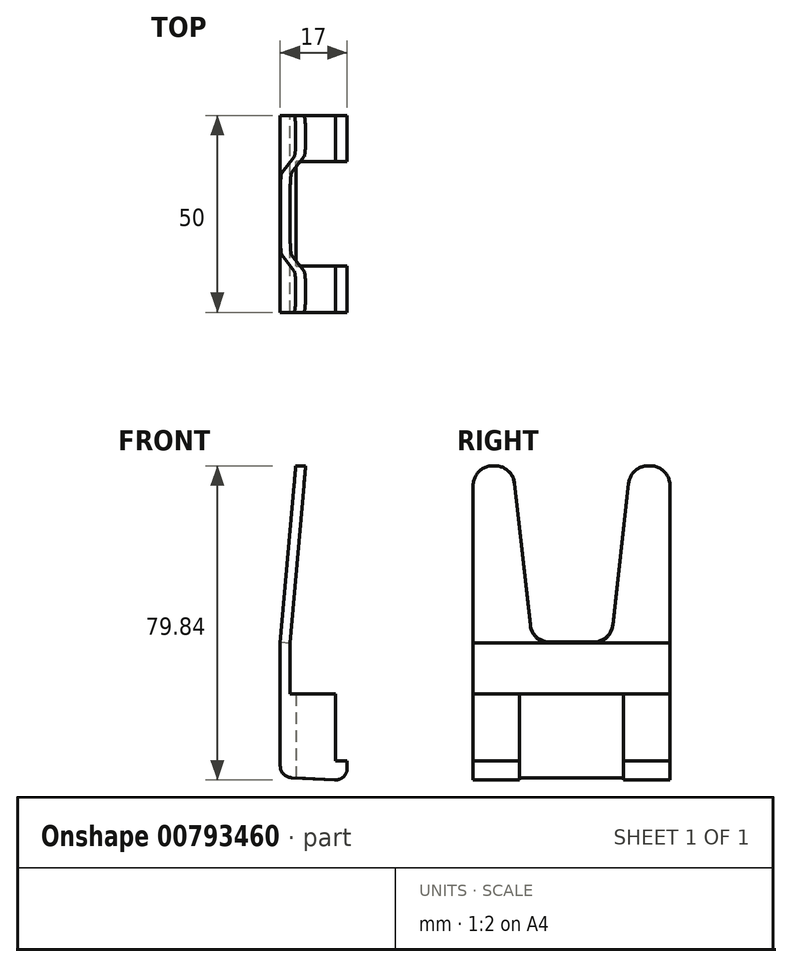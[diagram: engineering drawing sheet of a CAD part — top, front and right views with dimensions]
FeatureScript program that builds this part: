
annotation { "Feature Type Name" : "Feature", "Feature Type Description" : "" }
export const myFeature = defineFeature(function(context is Context, id is Id, definition is map)
    precondition{}
    {
        {
            var Q0;
            Q0=qCreatedBy(makeId("Front.planeOp"),FACE);
            var sketch = newSketch(context, id + "F0", { "sketchPlane" : qUnion([Q0])});
            skLineSegment(sketch, "E0", {"start": v(0, 0.9) * mm, "end": v(0, 35) * mm});
            skLineSegment(sketch, "E1", {"start": v(2.5, 35) * mm, "end": v(2.5, 22) * mm});
            skLineSegment(sketch, "E2", {"start": v(2.5, 22) * mm, "end": v(14, 22) * mm});
            skLineSegment(sketch, "E3", {"start": v(14, 22) * mm, "end": v(14, 5) * mm});
            skLineSegment(sketch, "E4", {"start": v(14, 5) * mm, "end": v(17, 5) * mm});
            skLineSegment(sketch, "E5", {"start": v(17, 5) * mm, "end": v(17, 0) * mm});
            skLineSegment(sketch, "E6", {"start": v(17, 0) * mm, "end": v(0, 0.9) * mm});
            skLineSegment(sketch, "E7", {"start": v(-12.07, 35) * mm, "end": v(18.84, 35) * mm, "construction": true});
            skLineSegment(sketch, "E8", {"start": v(0, 35) * mm, "end": v(3.94, 80) * mm});
            skLineSegment(sketch, "E9", {"start": v(3.94, 80) * mm, "end": v(6.44, 80) * mm});
            skLineSegment(sketch, "E10", {"start": v(6.44, 80) * mm, "end": v(2.5, 35) * mm});
            skSolve(sketch);
        }
        {
            var Q0;
            Q0 = qSketchRegion(id + "F0", true);
            extrude(context, id + "F1", {"entities" : qUnion([Q0]), "depth" : 50 * mm, "offsetDistance" : 25 * mm});
        }
        {
            var Q0;
            Q0=makeQuery(id+"F1.opExtrude","SWEPT_FACE",FACE,{"disambiguationData":[OSD([sQuery(id+"F0.wireOp",EDGE,"E5")])]});
            var sketch = newSketch(context, id + "F2", { "sketchPlane" : qUnion([Q0])});
            skLineSegment(sketch, "E11.bottom", {"start": v(-11.75, 34.94) * mm, "end": v(-38.25, 34.94) * mm});
            skLineSegment(sketch, "E11.top", {"start": v(-11.75, -24.94) * mm, "end": v(-38.25, -24.94) * mm});
            skLineSegment(sketch, "E11.left", {"start": v(-11.75, 34.94) * mm, "end": v(-11.75, -24.94) * mm});
            skLineSegment(sketch, "E11.right", {"start": v(-38.25, 34.94) * mm, "end": v(-38.25, -24.94) * mm});
            skPoint(sketch, "E11.middle", {"position": v(-25, 5) * mm});
            skSolve(sketch);
        }
        {
            var Q0;
            {var subQ0=sQuery(id+"F2.wireOp",EDGE,"E11.bottom");Q0=makeQuery(id+"F2.imprint","IMPRINT",FACE,{"disambiguationData":[TD([[makeQuery(id+"F2.imprint","IMPRINT",EDGE,{"derivedFrom":subQ0}),1.0]])]});}
            var Q1;
            {var subQ0=sQuery(id+"F2.wireOp",EDGE,"E11.left");var subQ1=sQuery(id+"F0.wireOp",EDGE,"E5");var subQ2=makeQuery(id+"F1.opExtrude","SWEPT_EDGE",EDGE,{"disambiguationData":[OSD([sQuery(id+"F0.wireOp",EDGE,"E4"),subQ1])]});var subQ3=makeQuery(id+"F2.imprint","INTERSECT",VERTEX,{"derivedFrom":[subQ2,subQ0]});Q1=makeQuery(id+"F2.imprint","IMPRINT",FACE,{"disambiguationData":[TD([[makeQuery(id+"F2.imprint","IMPRINT",EDGE,{"disambiguationData":[TD([[subQ3,-1.0]])],"derivedFrom":subQ0}),-1.0]])]});}
            extrude(context, id + "F3", {"entities" : qUnion([Q0, Q1]), "operationType" : NewBodyOperationType.REMOVE, "oppositeDirection" : true, "depth" : 13 * mm, "offsetDistance" : 25 * mm});
        }
        {
            var Q0;
            Q0=makeQuery(id+"F3.boolean.opBoolean","MERGE",FACE,{"derivedFrom":[makeQuery(id+"F1.opExtrude","SWEPT_FACE",FACE,{"disambiguationData":[OSD([sQuery(id+"F0.wireOp",EDGE,"E1")])]}),makeQuery(id+"F3.opExtrude","CAP_FACE",FACE,{"disambiguationData":[OSD([sQuery(id+"F0.wireOp",EDGE,"E5"),sQuery(id+"F0.wireOp",EDGE,"ma2ZBqUt-ZaSP-WYbq-Jd49-SRVpUCsUzQty"),sQuery(id+"F2.wireOp",EDGE,"E11.bottom"),sQuery(id+"F2.wireOp",EDGE,"E11.left"),sQuery(id+"F2.wireOp",EDGE,"E11.right")])],"isStart":false})]});
            var sketch = newSketch(context, id + "F4", { "sketchPlane" : qUnion([Q0])});
            skLineSegment(sketch, "E12", {"start": v(-15.42, 29.58) * mm, "end": v(-10, 35) * mm});
            skLineSegment(sketch, "E13", {"start": v(-25, 29.58) * mm, "end": v(-25, 92.21) * mm, "construction": true});
            skLineSegment(sketch, "E14.MirrorCS", {"start": v(-34.58, 29.58) * mm, "end": v(-40, 35) * mm});
            skLineSegment(sketch, "E15", {"start": v(-40, 35) * mm, "end": v(-10, 35) * mm});
            skLineSegment(sketch, "E16", {"start": v(-34.58, 29.58) * mm, "end": v(-15.42, 29.58) * mm});
            skPoint(sketch, "E17.orphan", {"position": v(-35, 30) * mm});
            skPoint(sketch, "E18.end.orphan", {"position": v(-15, 30) * mm});
            skPoint(sketch, "E19.MirrorCS.start.orphan", {"position": v(-25, 30) * mm});
            skSolve(sketch);
        }
        {
            var Q0;
            Q0=makeQuery(id+"F1.opExtrude","SWEPT_EDGE",EDGE,{"disambiguationData":[OSD([sQuery(id+"F0.wireOp",EDGE,"E0"),sQuery(id+"F0.wireOp",EDGE,"E6")])]});
            var Q1;
            {var subQ0=sQuery(id+"F0.wireOp",EDGE,"E6");var subQ1=sQuery(id+"F0.wireOp",EDGE,"E5");Q1=makeQuery(id+"F3.boolean.opBoolean","SPLIT",EDGE,{"disambiguationData":[TD([makeQuery(id+"F3.opExtrude","SWEPT_FACE",FACE,{"disambiguationData":[OSD([sQuery(id+"F2.wireOp",EDGE,"E11.right")])]})])],"derivedFrom":makeQuery(id+"F1.opExtrude","SWEPT_EDGE",EDGE,{"disambiguationData":[OSD([subQ1,subQ0])]})});}
            var Q2;
            {var subQ0=sQuery(id+"F0.wireOp",EDGE,"E6");var subQ1=sQuery(id+"F0.wireOp",EDGE,"E5");Q2=makeQuery(id+"F3.boolean.opBoolean","SPLIT",EDGE,{"disambiguationData":[TD([makeQuery(id+"F3.opExtrude","SWEPT_FACE",FACE,{"disambiguationData":[OSD([sQuery(id+"F2.wireOp",EDGE,"E11.left")])]})])],"derivedFrom":makeQuery(id+"F1.opExtrude","SWEPT_EDGE",EDGE,{"disambiguationData":[OSD([subQ1,subQ0])]})});}
            fillet(context, id + "F5", {"entities" : qUnion([Q0, Q1, Q2]), "radius" : 3 * mm, "tangentPropagation" : true, "allowEdgeOverflow" : false});
        }
        {
            var Q0;
            Q0=makeQuery(id+"F1.opExtrude","SWEPT_FACE",FACE,{"disambiguationData":[OSD([sQuery(id+"F0.wireOp",EDGE,"E10")])]});
            var sketch = newSketch(context, id + "F6", { "sketchPlane" : qUnion([Q0])});
            skLineSegment(sketch, "E20", {"start": v(-35, 35.08) * mm, "end": v(-40, 80.26) * mm});
            skLineSegment(sketch, "E21.MirrorCS", {"start": v(-15, 35.08) * mm, "end": v(-10, 80.26) * mm});
            skSolve(sketch);
        }
        {
            var Q0;
            {var subQ0=sQuery(id+"F6.wireOp",EDGE,"E20");Q0=makeQuery(id+"F6.imprint","IMPRINT",FACE,{"disambiguationData":[TD([[makeQuery(id+"F6.imprint","IMPRINT",EDGE,{"derivedFrom":subQ0}),-1.0]])]});}
            extrude(context, id + "F7", {"entities" : qUnion([Q0]), "operationType" : NewBodyOperationType.REMOVE, "oppositeDirection" : true, "depth" : 25 * mm, "offsetDistance" : 25 * mm});
        }
        {
            var Q0;
            Q0=makeQuery(id+"F1.opExtrude","CAP_EDGE",EDGE,{"disambiguationData":[OSD([sQuery(id+"F0.wireOp",EDGE,"E9")])],"isStart":false});
            var Q1;
            Q1=makeQuery(id+"F7.boolean.opBoolean","INTERSECT",EDGE,{"derivedFrom":[makeQuery(id+"F1.opExtrude","SWEPT_FACE",FACE,{"disambiguationData":[OSD([sQuery(id+"F0.wireOp",EDGE,"E9")])]}),makeQuery(id+"F7.opExtrude","SWEPT_FACE",FACE,{"disambiguationData":[OSD([sQuery(id+"F6.wireOp",EDGE,"E20")])]})]});
            var Q2;
            Q2=makeQuery(id+"F7.boolean.opBoolean","INTERSECT",EDGE,{"derivedFrom":[makeQuery(id+"F1.opExtrude","SWEPT_FACE",FACE,{"disambiguationData":[OSD([sQuery(id+"F0.wireOp",EDGE,"E9")])]}),makeQuery(id+"F7.opExtrude","SWEPT_FACE",FACE,{"disambiguationData":[OSD([sQuery(id+"F6.wireOp",EDGE,"E21.MirrorCS")])]})]});
            var Q3;
            Q3=makeQuery(id+"F1.opExtrude","CAP_EDGE",EDGE,{"disambiguationData":[OSD([sQuery(id+"F0.wireOp",EDGE,"E9")])],"isStart":true});
            var Q4;
            Q4=makeQuery(id+"F7.boolean.opBoolean","COPY",EDGE,{"derivedFrom":makeQuery(id+"F7.opExtrude","SWEPT_EDGE",EDGE,{"disambiguationData":[OSD([sQuery(id+"F0.wireOp",EDGE,"E1"),sQuery(id+"F0.wireOp",EDGE,"E10"),sQuery(id+"F6.wireOp",EDGE,"E21.MirrorCS")])]})});
            var Q5;
            Q5=makeQuery(id+"F7.boolean.opBoolean","COPY",EDGE,{"derivedFrom":makeQuery(id+"F7.opExtrude","SWEPT_EDGE",EDGE,{"disambiguationData":[OSD([sQuery(id+"F0.wireOp",EDGE,"E1"),sQuery(id+"F0.wireOp",EDGE,"E10"),sQuery(id+"F6.wireOp",EDGE,"E20")])]})});
            fillet(context, id + "F8", {"entities" : qUnion([Q0, Q1, Q2, Q3, Q4, Q5]), "radius" : 5 * mm, "tangentPropagation" : true, "allowEdgeOverflow" : false});
        }
    });
